# Revit family: PipeFitting_XpressCu-Tee_female_Branch
name_source: partatom
category: Pipe Fittings
units: mm (PartAtom-declared; Revit-internal decimal feet)

## family parameters
Always vertical = Yes
Cut with Voids When Loaded = No
Part Type = Tee
Round Connector Dimension = Use Radius
Shared = No
Work Plane-Based = No

## types (1)
- BAM - Tee BSP Female Branch - Xpress - Cu
    AssetType = Fixed
    COBieRequirement = Yes
    Colour = Copper
    Cost = 0 $
    Dry Weight = 0.00 kg
    DurationUnit = Year
    Finish = Copper
    Lookup Table Name = Tee Female Branch - Xpress - Cu
    NominalHeight = 0 mm  [stored 0 ft]
    NominalLength = 0 mm  [stored 0 ft]
    NominalWidth = 0 mm  [stored 0 ft]
    Operating Weight = 0.00 kg
    ReplacementCost = 0
    RevitMaterial = Copper, Alloy
    Ring width = 5 mm  [stored 0.0164042 ft]
    ServiceLifeDuration = 0
    Shape = Tee
    Size = Varies
    WarrantyDurationLabor = 0
    WarrantyDurationParts = 0
    WarrantyDurationUnit = Year

note: [stored X ft] marks values corroborated as IEEE doubles in the binary element streams (Revit-internal decimal feet)

## geometry (parser evidence)
native form markers: Sweep x3
no freeform markers — native parametric forms only
